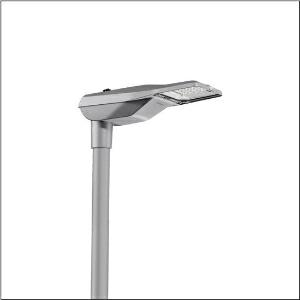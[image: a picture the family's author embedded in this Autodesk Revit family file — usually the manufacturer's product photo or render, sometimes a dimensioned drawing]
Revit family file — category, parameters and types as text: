
# Revit family: streetlight_sl_21_iq_micro___p0_8a_5xe1u31v08cb_453e
name_source: partatom
category: Lighting Fixtures
units: mm (PartAtom-declared; Revit-internal decimal feet)

## family parameters
Cut with Voids When Loaded = No
Host = Face
Light Source = No
Part Type = Normal
Room Calculation Point = No
Round Connector Dimension = Use Diameter
Shared = No

## types (1)
- --- (1 x LED, 2890 lm, 19.1 W, 3000K)
    Apparent Load = 19 VA
    CIE Flux Codes = 33 69 96 100 100
    Color Rendering = 70
    Color Temperature = 3000K
    Default Elevation = 1800 mm
    Description = Streetlight SL 21 iQ micro, mast luminaire, primary light control with lens, of PMMA, primary optical cover: cover, of toughened safety glass, transparent, light distribution: P0.8a, light emission: direct distribution, primary light characteristic: asymmetric, installation type: post-top, side-entry, LED, High Power LED, rated luminous flux: 2.890lm, luminous efficacy: 151lm/W, light colour: 730, colour temperature: 3000K, control gear: iQ-Street Remote, D4i with power reduction, control: pre-setting: logarithmic dimming characteristic, Street-Remote, Auto-Match, Temp-Guard, Lumen-Switch, Night-Set, Smart-Wire, Light-Fading, Desk-Remote (wireless, voltage-free reading and setting of iQ features in the workshop via application-optimized NFC function/RFID function), optimised constant luminous flux control (CLO 2.0), mains connection: 220..240V, AC, 50/60Hz, start of lifetime: 19W, end of service life: 20W, reduction: 9W, luminaire housing, of diecast aluminium, powder-coated, Siteco® metallic grey (DB 702S), corrosivity category C5 high according to DIN EN ISO 12944, please order mast flange separately, inclination adjustable: 0°, 5°, 10°, 15°, sealing non-destructively replaceable, multi-level sealing system, length: 528mm, width: 235mm, height: 110mm, mast flange for spigot size: 42mm (side-entry): 5XC10008XM4, 60/48mm (side-entry/post-top): 5XC10108XM2, 76/60mm (side-entry/post-top): 5XC10108XM1, mounting height: 4..8m, Smart Interface above, protection rating (complete): IP66, insulation class (complete): insulation class II (safety insulation), certification: CE, ENEC, ENEC+, VDE, impact resistance: IK10, permissible operating ambient temperature for outdoor applications: -40..+50°C, standard-compliant lighting for roads and squares, packaging unit: 1 piece

Light Distribution: P0.8a
    Height = 110 mm
    Lamp = 1 x LED
    Lamp Light Flux = 2890 lm
    Lamp Power = 19.1 W
    Lamp count = 1
    Length = 528 mm
    Luminous efficacy = 151 lm/W
    Manufacturer = Siteco
    ModVariant = No
    Model = 5XE1U31V08CB
    Number of Poles = 1
    OnlyDefault = Yes
    Power Factor = 1
    Product Name = Streetlight SL 21 iQ micro | P0.8a
    Product group = mast luminaire | pylon top
    ProductGroupID = 6100
    Protection Class = Protection class II
    Protection Degree = IP 66
    RLX_Detail_Level = 1
    RLX_Emergency_Light_Flux = 0 lm
    RLX_Emergency_Type = 0
    RLX_Emergency_Type_DB = No
    RlxData = <blob elided: 98081 chars, md5=d8467147>
    Socket = socket
    Standby Power = 0 W
    System Light Flux = 2890 lm
    System Power = 19 W
    Type Comments = factory setting: luminous flux: 100 % | dim-lin: 254 | 387 mA
    Type Image = l_1277292.jpg
    URL = http://relux.com
    VarID = @adj_083347
    Voltage = 0 V
    Weight = 0.00 kg
    Width = 235 mm

## geometry (parser evidence)
native form markers: Blend x4, Sweep x11
no freeform markers — native parametric forms only
